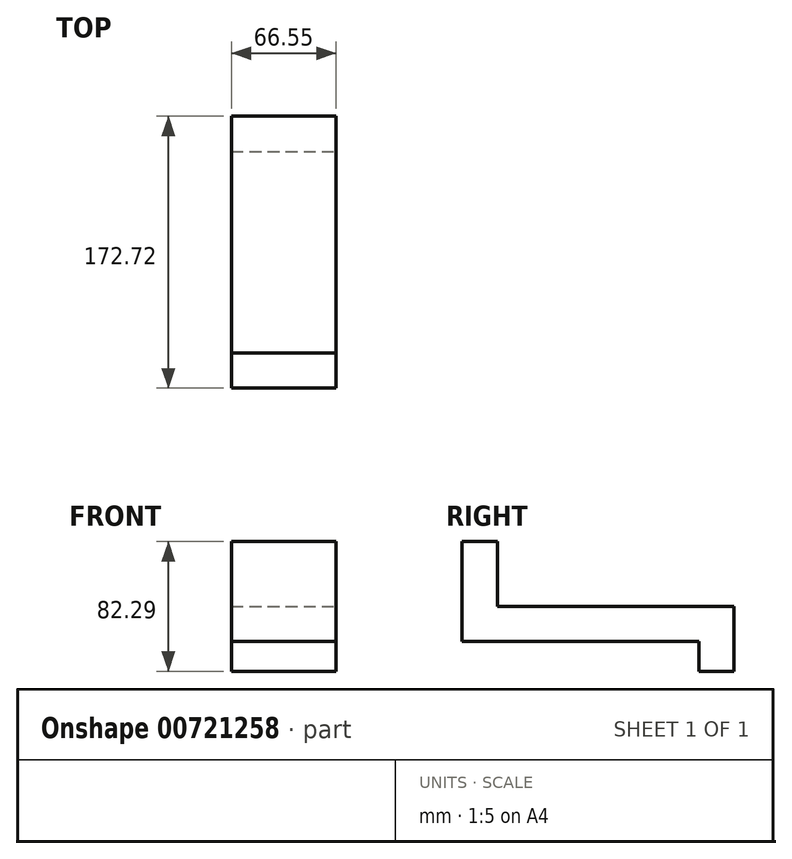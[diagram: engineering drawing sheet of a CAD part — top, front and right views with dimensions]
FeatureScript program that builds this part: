
annotation { "Feature Type Name" : "Feature", "Feature Type Description" : "" }
export const myFeature = defineFeature(function(context is Context, id is Id, definition is map)
    precondition{}
    {
        {
            var Q0;
            Q0=qCreatedBy(makeId("Right.planeOp"),FACE);
            var sketch = newSketch(context, id + "F0", { "sketchPlane" : qUnion([Q0])});
            skLineSegment(sketch, "E0", {"start": v(-61.2, 14.96) * mm, "end": v(-61.2, -48.54) * mm});
            skLineSegment(sketch, "E1", {"start": v(-61.2, -48.54) * mm, "end": v(89.17, -48.54) * mm});
            skLineSegment(sketch, "E2", {"start": v(89.17, -48.54) * mm, "end": v(89.17, -67.33) * mm});
            skLineSegment(sketch, "E3", {"start": v(89.17, -67.33) * mm, "end": v(111.53, -67.33) * mm});
            skLineSegment(sketch, "E4", {"start": v(111.53, -67.33) * mm, "end": v(111.53, -26.19) * mm});
            skLineSegment(sketch, "E5", {"start": v(111.53, -26.19) * mm, "end": v(-38.84, -26.19) * mm});
            skLineSegment(sketch, "E6", {"start": v(-38.84, -26.19) * mm, "end": v(-38.84, 14.96) * mm});
            skLineSegment(sketch, "E7", {"start": v(-38.84, 14.96) * mm, "end": v(-61.2, 14.96) * mm});
            skSolve(sketch);
        }
        {
            var Q0;
            Q0=makeQuery(id+"F0.imprint","IMPRINT",FACE,{"disambiguationData":[TD([[makeQuery(id+"F0.imprint","IMPRINT",EDGE,{"derivedFrom":sQuery(id+"F0.wireOp",EDGE,"E0")}),1.0]])]});
            extrude(context, id + "F1", {"entities" : qUnion([Q0]), "oppositeDirection" : true, "depth" : 66.55 * mm, "offsetDistance" : 25.4 * mm});
        }
    });
